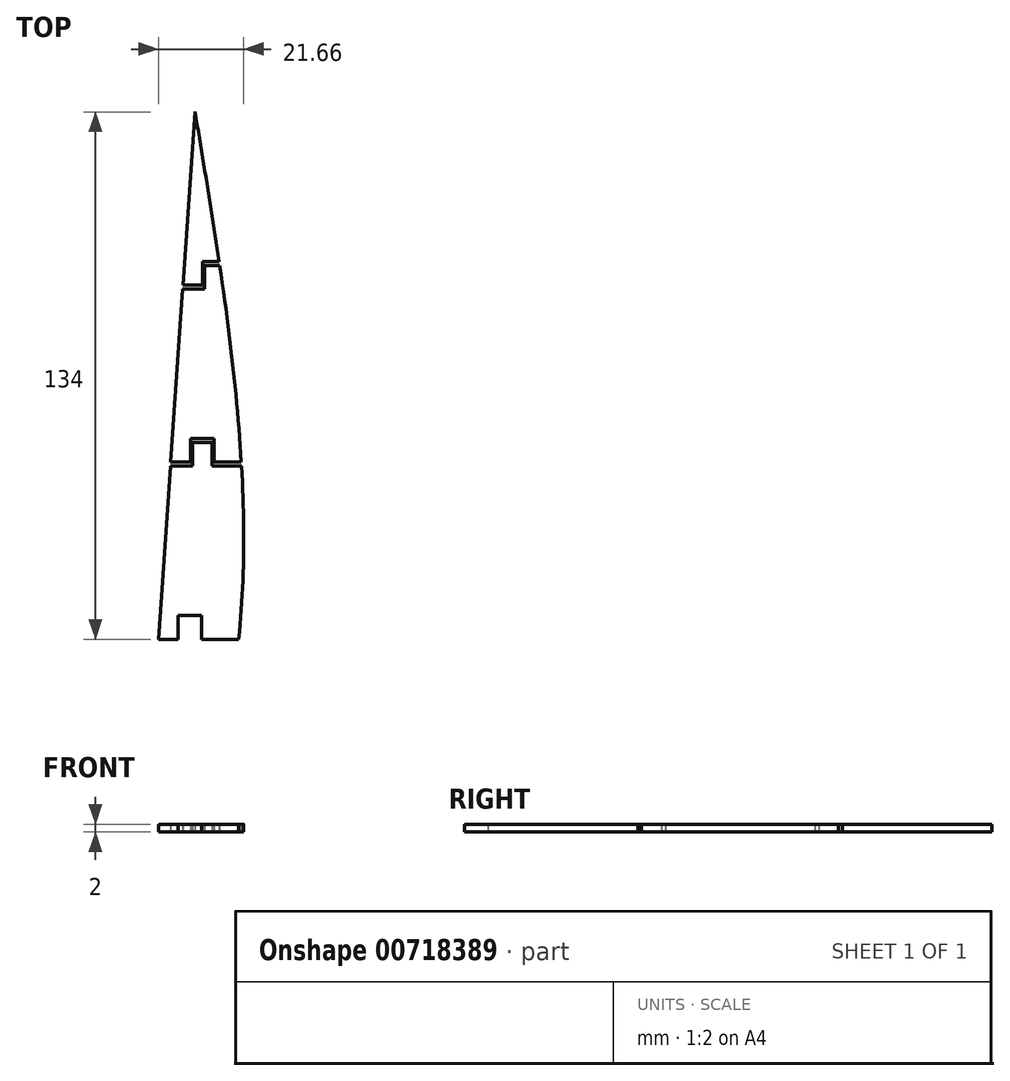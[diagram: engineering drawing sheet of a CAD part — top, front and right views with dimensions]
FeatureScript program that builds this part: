
annotation { "Feature Type Name" : "Feature", "Feature Type Description" : "" }
export const myFeature = defineFeature(function(context is Context, id is Id, definition is map)
    precondition{}
    {
        {
            var Q0;
            Q0=qCreatedBy(makeId("Top.planeOp"),FACE);
            var sketch = newSketch(context, id + "F0", { "sketchPlane" : qUnion([Q0])});
            skLineSegment(sketch, "E0", {"start": v(-40.75, 64.3) * mm, "end": v(-43.81, 20.3) * mm});
            skLineSegment(sketch, "E1", {"start": v(-43.81, 20.3) * mm, "end": v(-38.81, 20.3) * mm});
            skLineSegment(sketch, "E2", {"start": v(-46.94, -24.7) * mm, "end": v(-41.94, -24.7) * mm});
            skLineSegment(sketch, "E3", {"start": v(-50.07, -69.7) * mm, "end": v(-45.07, -69.7) * mm});
            skLineSegment(sketch, "E4.top", {"start": v(-38.81, 26.3) * mm, "end": v(-34.64, 26.3) * mm});
            skLineSegment(sketch, "E4.left", {"start": v(-38.81, 20.3) * mm, "end": v(-38.81, 26.3) * mm});
            skLineSegment(sketch, "E5.top", {"start": v(-41.94, -18.7) * mm, "end": v(-35.94, -18.7) * mm});
            skLineSegment(sketch, "E5.left", {"start": v(-41.94, -24.7) * mm, "end": v(-41.94, -18.7) * mm});
            skLineSegment(sketch, "E5.right", {"start": v(-35.94, -24.7) * mm, "end": v(-35.94, -18.7) * mm});
            skLineSegment(sketch, "E6.top", {"start": v(-45.07, -63.7) * mm, "end": v(-39.07, -63.7) * mm});
            skLineSegment(sketch, "E6.left", {"start": v(-45.07, -69.7) * mm, "end": v(-45.07, -63.7) * mm});
            skLineSegment(sketch, "E6.right", {"start": v(-39.07, -69.7) * mm, "end": v(-39.07, -63.7) * mm});
            skLineSegment(sketch, "E7", {"start": v(-43.88, 19.3) * mm, "end": v(-38.31, 19.3) * mm});
            skLineSegment(sketch, "E8", {"start": v(-47.01, -25.7) * mm, "end": v(-41.44, -25.7) * mm});
            skLineSegment(sketch, "E9.top", {"start": v(-38.31, 25.3) * mm, "end": v(-34.5, 25.3) * mm});
            skLineSegment(sketch, "E9.left", {"start": v(-38.31, 19.3) * mm, "end": v(-38.31, 25.3) * mm});
            skLineSegment(sketch, "E10.top", {"start": v(-41.44, -19.7) * mm, "end": v(-36.44, -19.7) * mm});
            skLineSegment(sketch, "E10.left", {"start": v(-41.44, -25.7) * mm, "end": v(-41.44, -19.7) * mm});
            skLineSegment(sketch, "E10.right", {"start": v(-36.44, -25.7) * mm, "end": v(-36.44, -19.7) * mm});
            skLineSegment(sketch, "E11.trimOffspring", {"start": v(-43.88, 19.3) * mm, "end": v(-46.94, -24.7) * mm});
            skLineSegment(sketch, "E12.trimOffspring", {"start": v(-47.01, -25.7) * mm, "end": v(-50.07, -69.7) * mm});
            skLineSegment(sketch, "E13.trimOffspring", {"start": v(-35.94, -24.7) * mm, "end": v(-29, -24.7) * mm});
            skLineSegment(sketch, "E14.trimOffspring", {"start": v(-36.44, -25.7) * mm, "end": v(-28.95, -25.7) * mm});
            skLineSegment(sketch, "E15.trimOffspring", {"start": v(-39.07, -69.7) * mm, "end": v(-29.68, -69.7) * mm});
            skFitSpline(sketch, "E16", {"points": [v(-40.75, 64.3) * mm, v(-29.68, -69.7) * mm, v(-60.96, -173.06) * mm], "startDerivative": vector(43.97, -263.42) * mm, "endDerivative": vector(-86.77, -210.32) * mm});
            skPoint(sketch, "E17.MirrorCS.start.orphan", {"position": v(-20.3, -69.7) * mm});
            skSolve(sketch);
        }
        {
            var Q0;
            Q0=makeQuery(id+"F0.imprint","IMPRINT",FACE,{"disambiguationData":[TD([[makeQuery(id+"F0.imprint","IMPRINT",EDGE,{"derivedFrom":sQuery(id+"F0.wireOp",EDGE,"E2")}),1.0]])]});
            var Q1;
            {var subQ1=sQuery(id+"F0.wireOp",EDGE,"E0");Q1=makeQuery(id+"F0.imprint","IMPRINT",FACE,{"disambiguationData":[TD([[makeQuery(id+"F0.imprint","IMPRINT",EDGE,{"derivedFrom":subQ1}),1.0]])]});}
            var Q2;
            Q2=makeQuery(id+"F0.imprint","IMPRINT",FACE,{"disambiguationData":[TD([[makeQuery(id+"F0.imprint","IMPRINT",EDGE,{"derivedFrom":sQuery(id+"F0.wireOp",EDGE,"E3")}),1.0]])]});
            var Q3;
            Q3=sQuery(id+"F0.wireOp",EDGE,"E5.top");
            var Q4;
            Q4=sQuery(id+"F0.wireOp",EDGE,"E2");
            var Q5;
            Q5=sQuery(id+"F0.wireOp",EDGE,"E7");
            var Q6;
            Q6=sQuery(id+"F0.wireOp",EDGE,"E6.right");
            var Q7;
            Q7=sQuery(id+"F0.wireOp",EDGE,"E0");
            var Q8;
            Q8=sQuery(id+"F0.wireOp",EDGE,"E3");
            var Q9;
            Q9=sQuery(id+"F0.wireOp",EDGE,"E1");
            var Q10;
            Q10=sQuery(id+"F0.wireOp",EDGE,"E6.left");
            var Q11;
            Q11=sQuery(id+"F0.wireOp",EDGE,"E5.right");
            var Q12;
            Q12=sQuery(id+"F0.wireOp",EDGE,"E6.top");
            var Q13;
            Q13=sQuery(id+"F0.wireOp",EDGE,"E14.trimOffspring");
            var Q14;
            Q14=sQuery(id+"F0.wireOp",EDGE,"E15.trimOffspring");
            var Q15;
            Q15=sQuery(id+"F0.wireOp",EDGE,"E12.trimOffspring");
            var Q16;
            Q16=sQuery(id+"F0.wireOp",EDGE,"E8");
            var Q17;
            Q17=sQuery(id+"F0.wireOp",EDGE,"E10.top");
            var Q18;
            Q18=sQuery(id+"F0.wireOp",EDGE,"E16");
            var Q19;
            Q19=sQuery(id+"F0.wireOp",EDGE,"E10.right");
            var Q20;
            Q20=sQuery(id+"F0.wireOp",EDGE,"E11.trimOffspring");
            var Q21;
            Q21=sQuery(id+"F0.wireOp",EDGE,"E13.trimOffspring");
            var Q22;
            Q22=sQuery(id+"F0.wireOp",EDGE,"E9.left");
            var Q23;
            Q23=sQuery(id+"F0.wireOp",EDGE,"E4.left");
            var Q24;
            Q24=sQuery(id+"F0.wireOp",EDGE,"E10.left");
            var Q25;
            Q25=sQuery(id+"F0.wireOp",EDGE,"E4.top");
            var Q26;
            Q26=sQuery(id+"F0.wireOp",EDGE,"E5.left");
            var Q27;
            Q27=sQuery(id+"F0.wireOp",EDGE,"E9.top");
            extrude(context, id + "F1", {"entities" : qUnion([Q0, Q1, Q2]), "surfaceEntities" : qUnion([Q3, Q4, Q5, Q6, Q7, Q8, Q9, Q10, Q11, Q12, Q13, Q14, Q15, Q16, Q17, Q18, Q19, Q20, Q21, Q22, Q23, Q24, Q25, Q26, Q27]), "depth" : 2 * mm, "offsetDistance" : 25 * mm});
        }
    });
